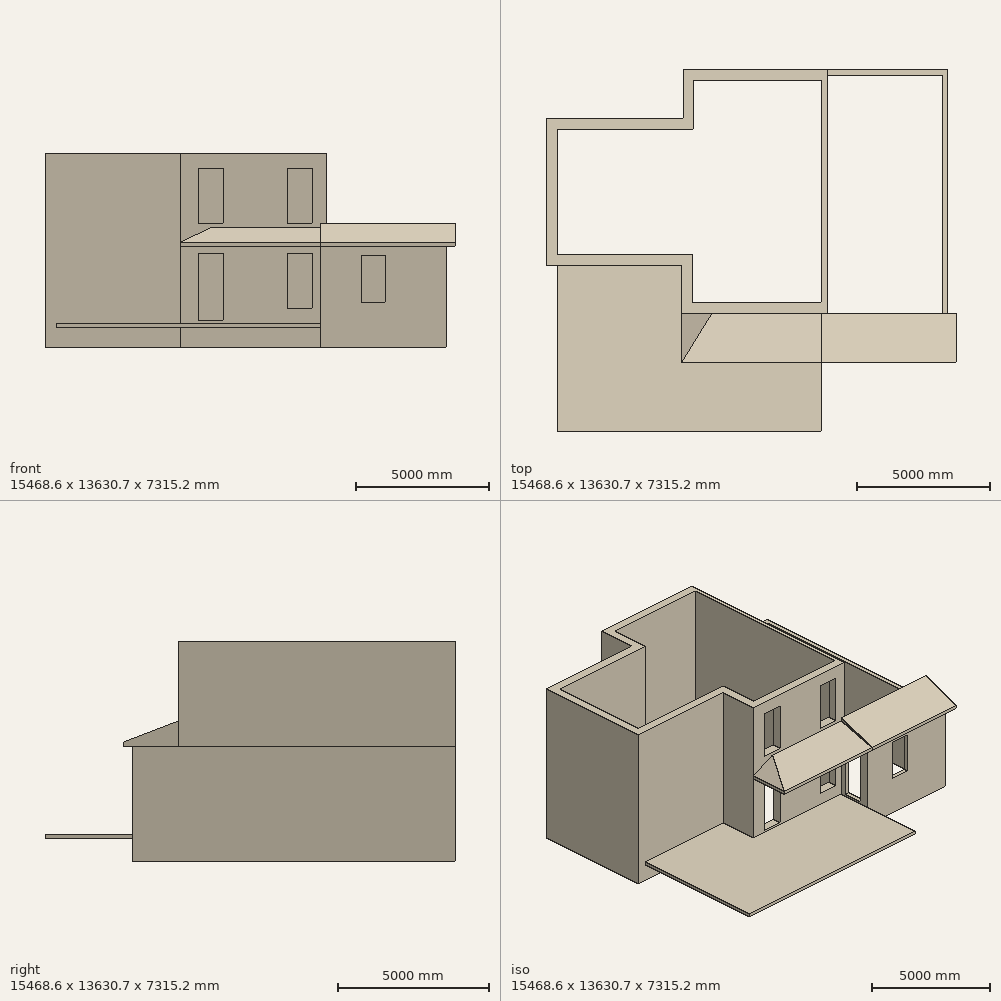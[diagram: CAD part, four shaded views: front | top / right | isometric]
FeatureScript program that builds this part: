
annotation { "Feature Type Name" : "Feature", "Feature Type Description" : "" }
export const myFeature = defineFeature(function(context is Context, id is Id, definition is map)
    precondition{}
    {
        {
            var Q0;
            Q0=qCreatedBy(makeId("Top.planeOp"),FACE);
            var sketch = newSketch(context, id + "F0", { "sketchPlane" : qUnion([Q0])});
            skLineSegment(sketch, "E0", {"start": v(2936.1, -1904.68) * mm, "end": v(-2347.1, -1904.68) * mm});
            skLineSegment(sketch, "E1", {"start": v(-2347.1, -1904.68) * mm, "end": v(-2347.1, -75.88) * mm});
            skLineSegment(sketch, "E2", {"start": v(-2347.1, -75.88) * mm, "end": v(-7452.5, -75.88) * mm});
            skLineSegment(sketch, "E3", {"start": v(-7452.5, -75.88) * mm, "end": v(-7452.5, 5461.32) * mm});
            skLineSegment(sketch, "E4", {"start": v(-2296.3, 7290.12) * mm, "end": v(7685.9, 7290.12) * mm});
            skLineSegment(sketch, "E5", {"start": v(7685.9, 7290.12) * mm, "end": v(7685.9, -3454.08) * mm});
            skLineSegment(sketch, "E6", {"start": v(7685.9, -3454.08) * mm, "end": v(2936.1, -3454.08) * mm});
            skLineSegment(sketch, "E7", {"start": v(2936.1, -3454.08) * mm, "end": v(2936.1, -1904.68) * mm});
            skLineSegment(sketch, "E8", {"start": v(-2296.3, 7290.12) * mm, "end": v(-2296.3, 5461.32) * mm});
            skLineSegment(sketch, "E9", {"start": v(-2296.3, 5461.32) * mm, "end": v(-7452.5, 5461.32) * mm});
            skLineSegment(sketch, "E10.bottom", {"start": v(-7452.5, 5461.32) * mm, "end": v(-2296.3, 5461.32) * mm});
            skLineSegment(sketch, "E10.top", {"start": v(-7452.5, 8991.92) * mm, "end": v(-2296.3, 8991.92) * mm});
            skLineSegment(sketch, "E10.left", {"start": v(-7452.5, 5461.32) * mm, "end": v(-7452.5, 8991.92) * mm});
            skLineSegment(sketch, "E10.right", {"start": v(-2296.3, 5461.32) * mm, "end": v(-2296.3, 8991.92) * mm});
            skLineSegment(sketch, "E11.0", {"start": v(-1940.7, 330.52) * mm, "end": v(-7046.1, 330.52) * mm});
            skLineSegment(sketch, "E11.1", {"start": v(-1940.7, -1498.28) * mm, "end": v(-1940.7, 330.52) * mm});
            skLineSegment(sketch, "E11.2", {"start": v(-7046.1, 330.52) * mm, "end": v(-7046.1, 5054.92) * mm});
            skLineSegment(sketch, "E11.3", {"start": v(2936.1, -1498.28) * mm, "end": v(-1940.7, -1498.28) * mm});
            skLineSegment(sketch, "E11.4", {"start": v(3139.3, -3250.88) * mm, "end": v(3139.3, -1498.28) * mm});
            skLineSegment(sketch, "E11.5", {"start": v(7482.7, -3250.88) * mm, "end": v(3139.3, -3250.88) * mm});
            skLineSegment(sketch, "E11.6", {"start": v(-7046.1, 5054.92) * mm, "end": v(-1889.9, 5054.92) * mm});
            skLineSegment(sketch, "E11.7", {"start": v(-1889.9, 6883.72) * mm, "end": v(-1889.9, 5054.92) * mm});
            skLineSegment(sketch, "E11.8", {"start": v(-1889.9, 6883.72) * mm, "end": v(2936.1, 6883.72) * mm});
            skLineSegment(sketch, "E11.9", {"start": v(7482.7, 7086.92) * mm, "end": v(7482.7, -3250.88) * mm});
            skLineSegment(sketch, "E12", {"start": v(3139.3, -1498.28) * mm, "end": v(3139.3, 7290.12) * mm});
            skLineSegment(sketch, "E13", {"start": v(2936.1, -1498.28) * mm, "end": v(2936.1, 6883.72) * mm});
            skLineSegment(sketch, "E14.trimOffspring", {"start": v(3139.3, 7086.92) * mm, "end": v(7482.7, 7086.92) * mm});
            skLineSegment(sketch, "E15", {"start": v(2936.1, -1904.68) * mm, "end": v(3139.3, -1904.68) * mm});
            skSolve(sketch);
        }
        {
            var Q0;
            Q0=makeQuery(id+"F0.imprint","IMPRINT",FACE,{"disambiguationData":[TD([[makeQuery(id+"F0.imprint","IMPRINT",EDGE,{"derivedFrom":sQuery(id+"F0.wireOp",EDGE,"E0")}),-1.0]])]});
            extrude(context, id + "F1", {"entities" : qUnion([Q0]), "depth" : 7315.2 * mm, "offsetDistance" : 25.4 * mm});
        }
        {
            var Q0;
            {var subQ3=sQuery(id+"F0.wireOp",EDGE,"E5");Q0=makeQuery(id+"F0.imprint","IMPRINT",FACE,{"disambiguationData":[TD([[makeQuery(id+"F0.imprint","IMPRINT",EDGE,{"derivedFrom":subQ3}),-1.0]])]});}
            extrude(context, id + "F2", {"entities" : qUnion([Q0]), "operationType" : NewBodyOperationType.ADD, "depth" : 3810 * mm, "offsetDistance" : 25.4 * mm});
        }
        {
            var Q0;
            Q0=makeQuery(id+"F1.opExtrude","SWEPT_FACE",FACE,{"disambiguationData":[OSD([sQuery(id+"F0.wireOp",EDGE,"E0"),sQuery(id+"F0.wireOp",EDGE,"E15")])]});
            var sketch = newSketch(context, id + "F3", { "sketchPlane" : qUnion([Q0])});
            skLineSegment(sketch, "E16.bottom", {"start": v(1691.5, 3556) * mm, "end": v(2605.9, 3556) * mm});
            skLineSegment(sketch, "E16.top", {"start": v(1691.5, 1473.2) * mm, "end": v(2605.9, 1473.2) * mm});
            skLineSegment(sketch, "E16.left", {"start": v(1691.5, 3556) * mm, "end": v(1691.5, 1473.2) * mm});
            skLineSegment(sketch, "E16.right", {"start": v(2605.9, 3556) * mm, "end": v(2605.9, 1473.2) * mm});
            skLineSegment(sketch, "E17.bottom", {"start": v(-1661.3, 3556) * mm, "end": v(-746.9, 3556) * mm});
            skLineSegment(sketch, "E17.top", {"start": v(-1661.3, 1016) * mm, "end": v(-746.9, 1016) * mm});
            skLineSegment(sketch, "E17.left", {"start": v(-1661.3, 3556) * mm, "end": v(-1661.3, 1016) * mm});
            skLineSegment(sketch, "E17.right", {"start": v(-746.9, 3556) * mm, "end": v(-746.9, 1016) * mm});
            skLineSegment(sketch, "E18.bottom", {"start": v(-1661.3, 6756.4) * mm, "end": v(-746.9, 6756.4) * mm});
            skLineSegment(sketch, "E18.top", {"start": v(-1661.3, 4673.6) * mm, "end": v(-746.9, 4673.6) * mm});
            skLineSegment(sketch, "E18.left", {"start": v(-1661.3, 6756.4) * mm, "end": v(-1661.3, 4673.6) * mm});
            skLineSegment(sketch, "E18.right", {"start": v(-746.9, 6756.4) * mm, "end": v(-746.9, 4673.6) * mm});
            skLineSegment(sketch, "E19.bottom", {"start": v(1691.5, 4673.6) * mm, "end": v(2605.9, 4673.6) * mm});
            skLineSegment(sketch, "E19.top", {"start": v(1691.5, 6756.4) * mm, "end": v(2605.9, 6756.4) * mm});
            skLineSegment(sketch, "E19.left", {"start": v(1691.5, 4673.6) * mm, "end": v(1691.5, 6756.4) * mm});
            skLineSegment(sketch, "E19.right", {"start": v(2605.9, 4673.6) * mm, "end": v(2605.9, 6756.4) * mm});
            skLineSegment(sketch, "E20.bottom", {"start": v(4460.1, 3479.8) * mm, "end": v(5374.5, 3479.8) * mm});
            skLineSegment(sketch, "E20.top", {"start": v(4460.1, 1701.8) * mm, "end": v(5374.5, 1701.8) * mm});
            skLineSegment(sketch, "E20.left", {"start": v(4460.1, 3479.8) * mm, "end": v(4460.1, 1701.8) * mm});
            skLineSegment(sketch, "E20.right", {"start": v(5374.5, 3479.8) * mm, "end": v(5374.5, 1701.8) * mm});
            skPoint(sketch, "E21.oppositeSnap0", {"position": v(4917.3, 1701.8) * mm});
            skLineSegment(sketch, "E21.bottom", {"start": v(4917.3, 1701.8) * mm, "end": v(4917.3, 1701.8) * mm});
            skLineSegment(sketch, "E21.top", {"start": v(4917.3, 0) * mm, "end": v(4917.3, 0) * mm});
            skSolve(sketch);
        }
        {
            var Q0;
            Q0=makeQuery(id+"F3.imprint","IMPRINT",FACE,{"disambiguationData":[TD([[makeQuery(id+"F3.imprint","IMPRINT",EDGE,{"derivedFrom":sQuery(id+"F3.wireOp",EDGE,"E18.bottom")}),-1.0]])]});
            var Q1;
            Q1=makeQuery(id+"F3.imprint","IMPRINT",FACE,{"disambiguationData":[TD([[makeQuery(id+"F3.imprint","IMPRINT",EDGE,{"derivedFrom":sQuery(id+"F3.wireOp",EDGE,"E19.bottom")}),1.0]])]});
            var Q2;
            Q2=makeQuery(id+"F3.imprint","IMPRINT",FACE,{"disambiguationData":[TD([[makeQuery(id+"F3.imprint","IMPRINT",EDGE,{"derivedFrom":sQuery(id+"F3.wireOp",EDGE,"E16.bottom")}),-1.0]])]});
            var Q3;
            Q3=makeQuery(id+"F3.imprint","IMPRINT",FACE,{"disambiguationData":[TD([[makeQuery(id+"F3.imprint","IMPRINT",EDGE,{"derivedFrom":sQuery(id+"F3.wireOp",EDGE,"E17.bottom")}),-1.0]])]});
            extrude(context, id + "F4", {"entities" : qUnion([Q0, Q1, Q2, Q3]), "operationType" : NewBodyOperationType.REMOVE, "endBound" : BoundingType.UP_TO_NEXT, "oppositeDirection" : true, "depth" : 25.4 * mm, "offsetDistance" : 25.4 * mm});
        }
        {
            var Q0;
            Q0=makeQuery(id+"F2.opExtrude","SWEPT_FACE",FACE,{"disambiguationData":[OSD([sQuery(id+"F0.wireOp",EDGE,"E6")])]});
            var sketch = newSketch(context, id + "F5", { "sketchPlane" : qUnion([Q0])});
            skLineSegment(sketch, "E22.bottom", {"start": v(4460.1, 3467.1) * mm, "end": v(5374.5, 3467.1) * mm});
            skLineSegment(sketch, "E22.top", {"start": v(4460.1, 1689.1) * mm, "end": v(5374.5, 1689.1) * mm});
            skLineSegment(sketch, "E22.left", {"start": v(4460.1, 3467.1) * mm, "end": v(4460.1, 1689.1) * mm});
            skLineSegment(sketch, "E22.right", {"start": v(5374.5, 3467.1) * mm, "end": v(5374.5, 1689.1) * mm});
            skSolve(sketch);
        }
        {
            var Q0;
            Q0=makeQuery(id+"F5.imprint","IMPRINT",FACE,{"disambiguationData":[TD([[makeQuery(id+"F5.imprint","IMPRINT",EDGE,{"derivedFrom":sQuery(id+"F5.wireOp",EDGE,"E22.bottom")}),-1.0]])]});
            extrude(context, id + "F6", {"entities" : qUnion([Q0]), "operationType" : NewBodyOperationType.REMOVE, "endBound" : BoundingType.UP_TO_NEXT, "oppositeDirection" : true, "depth" : 25.4 * mm, "offsetDistance" : 25.4 * mm});
        }
        {
            var Q0;
            Q0=makeQuery(id+"F2.opExtrude","SWEPT_FACE",FACE,{"disambiguationData":[OSD([sQuery(id+"F0.wireOp",EDGE,"E7")])]});
            var sketch = newSketch(context, id + "F7", { "sketchPlane" : qUnion([Q0])});
            skLineSegment(sketch, "E23.bottom", {"start": v(2158.68, 3556) * mm, "end": v(3073.08, 3556) * mm});
            skLineSegment(sketch, "E23.top", {"start": v(2158.68, 1016) * mm, "end": v(3073.08, 1016) * mm});
            skLineSegment(sketch, "E23.left", {"start": v(2158.68, 3556) * mm, "end": v(2158.68, 1016) * mm});
            skLineSegment(sketch, "E23.right", {"start": v(3073.08, 3556) * mm, "end": v(3073.08, 1016) * mm});
            skSolve(sketch);
        }
        {
            var Q0;
            Q0=makeQuery(id+"F7.imprint","IMPRINT",FACE,{"disambiguationData":[TD([[makeQuery(id+"F7.imprint","IMPRINT",EDGE,{"derivedFrom":sQuery(id+"F7.wireOp",EDGE,"E23.bottom")}),-1.0]])]});
            extrude(context, id + "F8", {"entities" : qUnion([Q0]), "operationType" : NewBodyOperationType.REMOVE, "endBound" : BoundingType.UP_TO_NEXT, "oppositeDirection" : true, "depth" : 25.4 * mm, "offsetDistance" : 25.4 * mm});
        }
        {
            var Q0;
            Q0=qCreatedBy(makeId("Top.planeOp"),FACE);
            var sketch = newSketch(context, id + "F9", { "sketchPlane" : qUnion([Q0])});
            skLineSegment(sketch, "E24", {"start": v(-7022.27, -75.88) * mm, "end": v(-7022.27, -6340.6) * mm});
            skLineSegment(sketch, "E25", {"start": v(-7022.27, -6340.6) * mm, "end": v(2936.1, -6340.6) * mm});
            skLineSegment(sketch, "E26", {"start": v(2936.1, -6340.6) * mm, "end": v(2936.1, -1904.68) * mm});
            skLineSegment(sketch, "E27", {"start": v(2936.1, -1904.68) * mm, "end": v(-2347.1, -1904.68) * mm});
            skLineSegment(sketch, "E28", {"start": v(-2347.1, -1904.68) * mm, "end": v(-2347.1, -75.88) * mm});
            skLineSegment(sketch, "E29", {"start": v(-2347.1, -75.88) * mm, "end": v(-7022.27, -75.88) * mm});
            skSolve(sketch);
        }
        {
            var Q0;
            Q0=makeQuery(id+"F9.imprint","IMPRINT",FACE,{"disambiguationData":[TD([[makeQuery(id+"F9.imprint","IMPRINT",EDGE,{"derivedFrom":sQuery(id+"F9.wireOp",EDGE,"E24")}),1.0]])]});
            extrude(context, id + "F10", {"entities" : qUnion([Q0]), "depth" : 914.4 * mm, "offsetDistance" : 25.4 * mm, "hasSecondDirection" : true, "secondDirectionOppositeDirection" : false, "secondDirectionDepth" : 762 * mm});
        }
        {
            var Q0;
            Q0=makeQuery(id+"F2.opExtrude","SWEPT_FACE",FACE,{"disambiguationData":[OSD([sQuery(id+"F0.wireOp",EDGE,"E7")])]});
            var sketch = newSketch(context, id + "F11", { "sketchPlane" : qUnion([Q0])});
            skLineSegment(sketch, "E30", {"start": v(1904.68, 3810) * mm, "end": v(1904.68, 4673.6) * mm});
            skLineSegment(sketch, "E31", {"start": v(1904.68, 4673.6) * mm, "end": v(3758.88, 3962.4) * mm});
            skLineSegment(sketch, "E32", {"start": v(3758.88, 3962.4) * mm, "end": v(3758.88, 3810) * mm});
            skLineSegment(sketch, "E33", {"start": v(3758.88, 3810) * mm, "end": v(1904.68, 3810) * mm});
            skLineSegment(sketch, "E34", {"start": v(1904.68, 4521.2) * mm, "end": v(3758.88, 3962.4) * mm});
            skSolve(sketch);
        }
        {
            var Q0;
            {var subQ4=sQuery(id+"F11.wireOp",EDGE,"E30");Q0=makeQuery(id+"F11.imprint","IMPRINT",FACE,{"disambiguationData":[TD([[makeQuery(id+"F11.imprint","IMPRINT",EDGE,{"derivedFrom":subQ4}),-1.0]])]});}
            var Q1;
            {var subQ3=sQuery(id+"F11.wireOp",EDGE,"E32");Q1=makeQuery(id+"F11.imprint","IMPRINT",FACE,{"disambiguationData":[TD([[makeQuery(id+"F11.imprint","IMPRINT",EDGE,{"derivedFrom":subQ3}),-1.0]])]});}
            extrude(context, id + "F12", {"entities" : qUnion([Q0, Q1]), "oppositeDirection" : true, "depth" : 5080 * mm, "offsetDistance" : 25.4 * mm});
        }
        {
            var Q0;
            {var subQ3=sQuery(id+"F11.wireOp",EDGE,"E32");Q0=makeQuery(id+"F11.imprint","IMPRINT",FACE,{"disambiguationData":[TD([[makeQuery(id+"F11.imprint","IMPRINT",EDGE,{"derivedFrom":subQ3}),-1.0]])]});}
            var Q1;
            Q1=makeQuery(id+"F1.opExtrude","SWEPT_FACE",FACE,{"disambiguationData":[OSD([sQuery(id+"F0.wireOp",EDGE,"E1")])]});
            extrude(context, id + "F13", {"entities" : qUnion([Q0]), "endBound" : BoundingType.UP_TO_SURFACE, "depth" : 4064 * mm, "endBoundEntityFace" : qUnion([Q1]), "offsetDistance" : 25.4 * mm});
        }
        {
            var Q0;
            Q0=makeQuery(id+"F1.opExtrude","SWEPT_FACE",FACE,{"disambiguationData":[OSD([sQuery(id+"F0.wireOp",EDGE,"E0"),sQuery(id+"F0.wireOp",EDGE,"E15")])]});
            var sketch = newSketch(context, id + "F14", { "sketchPlane" : qUnion([Q0])});
            skLineSegment(sketch, "E35", {"start": v(-2347.1, 3962.4) * mm, "end": v(-1204.1, 3962.4) * mm});
            skPoint(sketch, "E35.endSnap0", {"position": v(-1204.1, 4673.6) * mm});
            skLineSegment(sketch, "E36", {"start": v(-1204.1, 3962.4) * mm, "end": v(-1204.1, 4521.2) * mm});
            skLineSegment(sketch, "E37", {"start": v(-1204.1, 4521.2) * mm, "end": v(-2347.1, 3962.4) * mm});
            skSolve(sketch);
        }
        {
            var Q0;
            Q0=makeQuery(id+"F14.imprint","IMPRINT",FACE,{"disambiguationData":[TD([[makeQuery(id+"F14.imprint","IMPRINT",EDGE,{"derivedFrom":sQuery(id+"F14.wireOp",EDGE,"E35")}),1.0]])]});
            var Q1;
            Q1=makeQuery(id+"F12.opExtrude","SWEPT_FACE",FACE,{"disambiguationData":[OSD([sQuery(id+"F11.wireOp",EDGE,"E32")])]});
            extrude(context, id + "F15", {"entities" : qUnion([Q0]), "endBound" : BoundingType.UP_TO_SURFACE, "depth" : 25.4 * mm, "endBoundEntityFace" : qUnion([Q1]), "offsetDistance" : 25.4 * mm});
        }
        {
            var Q0;
            Q0=makeQuery(id+"F13.opExtrude","SWEPT_BODY",BODY,{"disambiguationData":[OSD([sQuery(id+"F11.wireOp",EDGE,"E30"),sQuery(id+"F11.wireOp",EDGE,"E32"),sQuery(id+"F11.wireOp",EDGE,"E33"),sQuery(id+"F11.wireOp",EDGE,"E34")])]});
            var Q1;
            Q1=makeQuery(id+"F15.opExtrude","SWEPT_BODY",BODY,{"disambiguationData":[OSD([sQuery(id+"F14.wireOp",EDGE,"E35"),sQuery(id+"F14.wireOp",EDGE,"E36"),sQuery(id+"F14.wireOp",EDGE,"E37")])]});
            var Q2;
            Q2=makeQuery(id+"F13.opExtrude","SWEPT_BODY",BODY,{"disambiguationData":[OSD([sQuery(id+"F11.wireOp",EDGE,"E30"),sQuery(id+"F11.wireOp",EDGE,"E32"),sQuery(id+"F11.wireOp",EDGE,"E33"),sQuery(id+"F11.wireOp",EDGE,"E34")])]});
            var Q3;
            Q3=makeQuery(id+"F15.opExtrude","SWEPT_BODY",BODY,{"disambiguationData":[OSD([sQuery(id+"F14.wireOp",EDGE,"E35"),sQuery(id+"F14.wireOp",EDGE,"E36"),sQuery(id+"F14.wireOp",EDGE,"E37")])]});
            booleanBodies(context, id + "F16", {"operationType" : BooleanOperationType.INTERSECTION, "tools" : qUnion([Q0, Q1]), "targets" : qUnion([Q2, Q3])});
        }
        {
            var Q0;
            Q0=makeQuery(id+"F15.opExtrude","SWEPT_FACE",FACE,{"disambiguationData":[OSD([sQuery(id+"F14.wireOp",EDGE,"E36")])]});
            var Q1;
            Q1=makeQuery(id+"F12.opExtrude","CAP_FACE",FACE,{"disambiguationData":[OSD([sQuery(id+"F11.wireOp",EDGE,"E30"),sQuery(id+"F11.wireOp",EDGE,"E31"),sQuery(id+"F11.wireOp",EDGE,"E32"),sQuery(id+"F11.wireOp",EDGE,"E33")])],"isStart":true});
            extrude(context, id + "F17", {"entities" : qUnion([Q0]), "operationType" : NewBodyOperationType.ADD, "endBound" : BoundingType.UP_TO_SURFACE, "depth" : 25.4 * mm, "endBoundEntityFace" : qUnion([Q1]), "offsetDistance" : 25.4 * mm});
        }
        {
            var Q0;
            {var subQ0=sQuery(id+"F14.wireOp",EDGE,"E35");Q0=makeQuery(id+"F17.boolean.opBoolean","MERGE",FACE,{"derivedFrom":[makeQuery(id+"F15.opExtrude","SWEPT_FACE",FACE,{"disambiguationData":[OSD([subQ0])]}),makeQuery(id+"F17.opExtrude","SWEPT_FACE",FACE,{"disambiguationData":[OSD([subQ0,sQuery(id+"F14.wireOp",EDGE,"E36")])]})]});}
            var Q1;
            Q1=makeQuery(id+"F12.opExtrude","SWEPT_FACE",FACE,{"disambiguationData":[OSD([sQuery(id+"F11.wireOp",EDGE,"E33")])]});
            extrude(context, id + "F18", {"entities" : qUnion([Q0]), "endBound" : BoundingType.UP_TO_SURFACE, "depth" : 25.4 * mm, "endBoundEntityFace" : qUnion([Q1]), "offsetDistance" : 25.4 * mm});
        }
    });
